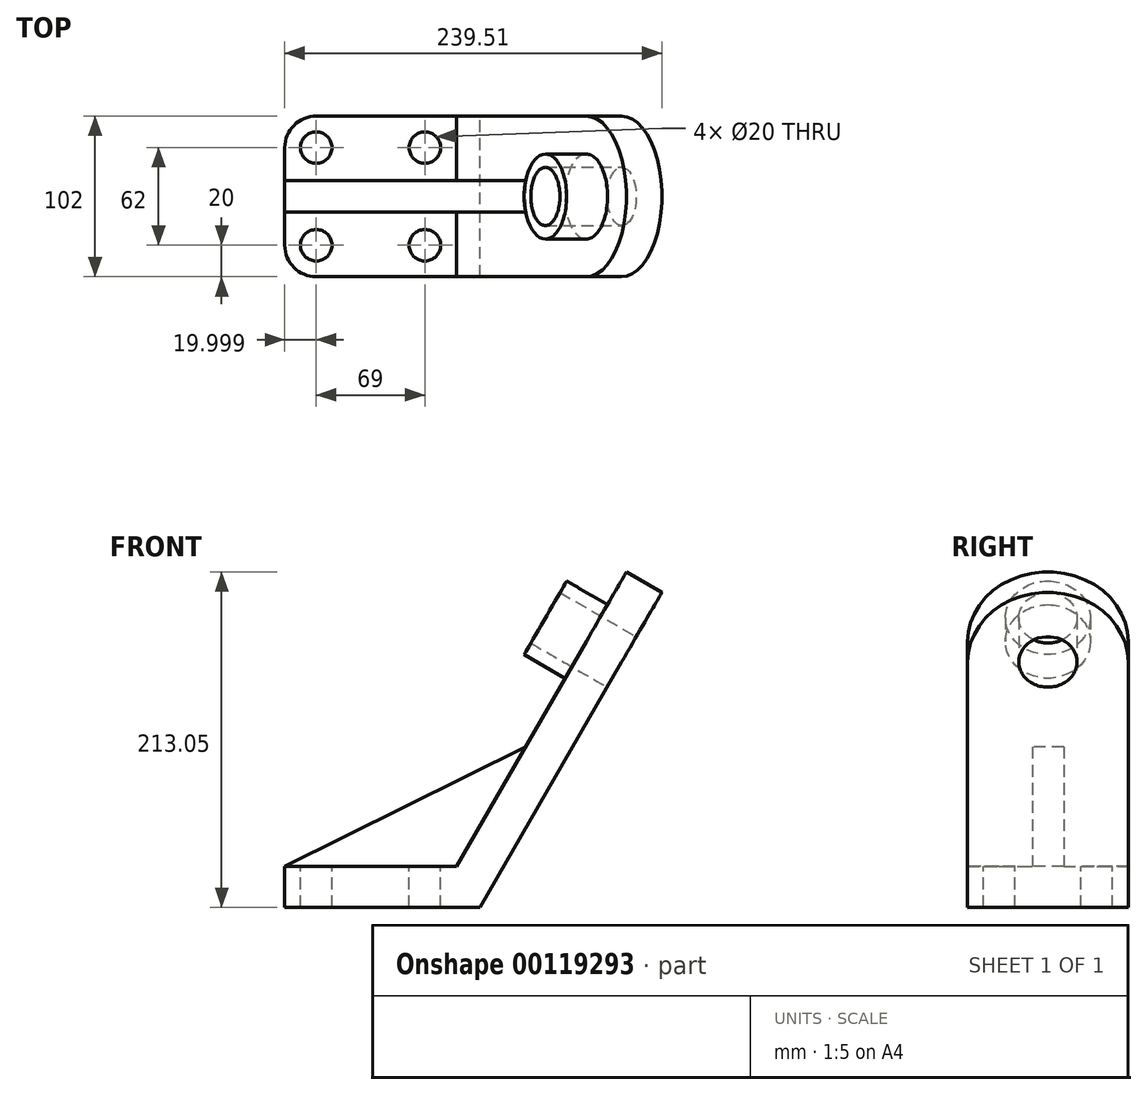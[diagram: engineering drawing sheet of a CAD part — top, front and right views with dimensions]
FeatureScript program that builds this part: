
annotation { "Feature Type Name" : "Feature", "Feature Type Description" : "" }
export const myFeature = defineFeature(function(context is Context, id is Id, definition is map)
    precondition{}
    {
        {
            var Q0;
            Q0=qCreatedBy(makeId("Front.planeOp"),FACE);
            var sketch = newSketch(context, id + "F0", { "sketchPlane" : qUnion([Q0])});
            skLineSegment(sketch, "E0", {"start": v(-124.01, -63.94) * mm, "end": v(-15.01, -63.94) * mm});
            skLineSegment(sketch, "E1", {"start": v(-15.01, -63.94) * mm, "end": v(92.98, 123.11) * mm});
            skLineSegment(sketch, "E2", {"start": v(115.5, 110.11) * mm, "end": v(0, -89.94) * mm});
            skLineSegment(sketch, "E3", {"start": v(0, -89.94) * mm, "end": v(-124.01, -89.94) * mm});
            skLineSegment(sketch, "E4", {"start": v(-124.01, -63.94) * mm, "end": v(-124.01, -89.94) * mm});
            skLineSegment(sketch, "E5", {"start": v(92.98, 123.11) * mm, "end": v(115.5, 110.11) * mm});
            skSolve(sketch);
        }
        {
            var Q0;
            Q0 = qSketchRegion(id + "F0", true);
            extrude(context, id + "F1", {"entities" : qUnion([Q0]), "depth" : 102 * mm});
        }
        {
            var Q0;
            Q0=makeQuery(id+"F1.opExtrude","CAP_EDGE",EDGE,{"disambiguationData":[OSD([sQuery(id+"F0.wireOp",EDGE,"E5")])],"isStart":true});
            var Q1;
            Q1=makeQuery(id+"F1.opExtrude","CAP_EDGE",EDGE,{"disambiguationData":[OSD([sQuery(id+"F0.wireOp",EDGE,"E5")])],"isStart":false});
            fillet(context, id + "F2", {"entities" : qUnion([Q0, Q1]), "radius" : 51 * mm, "tangentPropagation" : true, "allowEdgeOverflow" : false});
        }
        {
            var Q0;
            Q0=makeQuery(id+"F1.opExtrude","SWEPT_FACE",FACE,{"disambiguationData":[OSD([sQuery(id+"F0.wireOp",EDGE,"E1")])]});
            var sketch = newSketch(context, id + "F3", { "sketchPlane" : qUnion([Q0])});
            skCircle(sketch, "E6", {"center": v(51, 102.1) * mm, "radius": 18.5 * mm});
            skLineSegment(sketch, "E7", {"start": v(0, 102.1) * mm, "end": v(102, 102.1) * mm, "construction": true});
            skCircle(sketch, "E8", {"center": v(51, 102.1) * mm, "radius": 27 * mm});
            skSolve(sketch);
        }
        {
            var Q0;
            Q0 = qSketchRegion(id + "F3", true);
            extrude(context, id + "F4", {"entities" : qUnion([Q0]), "operationType" : NewBodyOperationType.ADD, "depth" : 30 * mm});
        }
        {
            var Q0;
            Q0=makeQuery(id+"F4.boolean.opBoolean","SPLIT",FACE,{"disambiguationData":[TD([makeQuery(id+"F4.opExtrude","SWEPT_FACE",FACE,{"disambiguationData":[OSD([sQuery(id+"F3.wireOp",EDGE,"E6")])]})])],"derivedFrom":makeQuery(id+"F1.opExtrude","SWEPT_FACE",FACE,{"disambiguationData":[OSD([sQuery(id+"F0.wireOp",EDGE,"E1")])]})});
            var sketch = newSketch(context, id + "F5", { "sketchPlane" : qUnion([Q0])});
            skCircle(sketch, "E9.0.0", {"center": v(51, 102.1) * mm, "radius": 18.5 * mm});
            skSolve(sketch);
        }
        {
            var Q0;
            Q0 = qSketchRegion(id + "F5", true);
            extrude(context, id + "F6", {"entities" : qUnion([Q0]), "operationType" : NewBodyOperationType.REMOVE, "oppositeDirection" : true, "depth" : 30 * mm});
        }
        {
            var Q0;
            Q0=makeQuery(id+"F1.opExtrude","CAP_FACE",FACE,{"disambiguationData":[OSD([sQuery(id+"F0.wireOp",EDGE,"E0"),sQuery(id+"F0.wireOp",EDGE,"E1"),sQuery(id+"F0.wireOp",EDGE,"E2"),sQuery(id+"F0.wireOp",EDGE,"E3"),sQuery(id+"F0.wireOp",EDGE,"E4"),sQuery(id+"F0.wireOp",EDGE,"E5")])],"isStart":true});
            cPlane(context, id + "F7", {"entities" : qUnion([Q0]), "cplaneType" : CPlaneType.OFFSET, "offset" : 51 * mm, "oppositeDirection" : true, "width" : 150 * mm, "height" : 150 * mm});
        }
        {
            var Q0;
            Q0=qCreatedBy(id+"F7.planeOp",FACE);
            var sketch = newSketch(context, id + "F8", { "sketchPlane" : qUnion([Q0])});
            skLineSegment(sketch, "E10", {"start": v(15.01, -63.94) * mm, "end": v(124.01, -63.94) * mm});
            skLineSegment(sketch, "E11.0.2", {"start": v(-28.87, 12.06) * mm, "end": v(15.01, -63.94) * mm});
            skLineSegment(sketch, "E12", {"start": v(15.01, -63.94) * mm, "end": v(-28.87, 12.06) * mm});
            skLineSegment(sketch, "E13", {"start": v(124.01, -63.94) * mm, "end": v(-28.87, 12.06) * mm});
            skPoint(sketch, "E11.0.1.end.orphan", {"position": v(-67.48, 78.94) * mm});
            skPoint(sketch, "E11.0.0.end.orphan", {"position": v(-90, 65.94) * mm});
            skPoint(sketch, "E11.0.5.end.orphan", {"position": v(0, -89.94) * mm});
            skPoint(sketch, "E11.0.4.end.orphan", {"position": v(124.01, -89.94) * mm});
            skSolve(sketch);
        }
        {
            var Q0;
            Q0 = qSketchRegion(id + "F8", true);
            extrude(context, id + "F9", {"entities" : qUnion([Q0]), "operationType" : NewBodyOperationType.ADD, "endBound" : BoundingType.SYMMETRIC, "depth" : 20 * mm});
        }
        {
            var Q0;
            {var subQ1=sQuery(id+"F0.wireOp",EDGE,"E4");var subQ2=sQuery(id+"F0.wireOp",EDGE,"E1");var subQ3=sQuery(id+"F0.wireOp",EDGE,"E0");Q0=makeQuery(id+"F9.boolean.opBoolean","SPLIT",FACE,{"disambiguationData":[TD([makeQuery(id+"F1.opExtrude","CAP_FACE",FACE,{"disambiguationData":[OSD([subQ3,subQ2,sQuery(id+"F0.wireOp",EDGE,"E2"),sQuery(id+"F0.wireOp",EDGE,"E3"),subQ1,sQuery(id+"F0.wireOp",EDGE,"E5")])],"isStart":true})])],"derivedFrom":makeQuery(id+"F1.opExtrude","SWEPT_FACE",FACE,{"disambiguationData":[OSD([subQ3])]})});}
            var sketch = newSketch(context, id + "F10", { "sketchPlane" : qUnion([Q0])});
            skCircle(sketch, "E14", {"center": v(-104.01, -20) * mm, "radius": 10 * mm});
            skCircle(sketch, "E15.0.1.0", {"center": v(-104.01, -82) * mm, "radius": 10 * mm});
            skCircle(sketch, "E15.1.0.0", {"center": v(-35.01, -20) * mm, "radius": 10 * mm});
            skCircle(sketch, "E15.1.1.0", {"center": v(-35.01, -82) * mm, "radius": 10 * mm});
            skLineSegment(sketch, "E15.direction1", {"start": v(-104.01, -20) * mm, "end": v(-35.01, -20) * mm, "construction": true});
            skLineSegment(sketch, "E15.direction2", {"start": v(-104.01, -20) * mm, "end": v(-104.01, -82) * mm, "construction": true});
            skSolve(sketch);
        }
        {
            var Q0;
            Q0 = qSketchRegion(id + "F10", true);
            extrude(context, id + "F11", {"entities" : qUnion([Q0]), "operationType" : NewBodyOperationType.REMOVE, "oppositeDirection" : true, "depth" : 30 * mm});
        }
        {
            var Q0;
            Q0=makeQuery(id+"F1.opExtrude","CAP_EDGE",EDGE,{"disambiguationData":[OSD([sQuery(id+"F0.wireOp",EDGE,"E4")])],"isStart":true});
            var Q1;
            Q1=makeQuery(id+"F1.opExtrude","CAP_EDGE",EDGE,{"disambiguationData":[OSD([sQuery(id+"F0.wireOp",EDGE,"E4")])],"isStart":false});
            fillet(context, id + "F12", {"entities" : qUnion([Q0, Q1]), "radius" : 20 * mm, "tangentPropagation" : true, "allowEdgeOverflow" : false});
        }
    });
